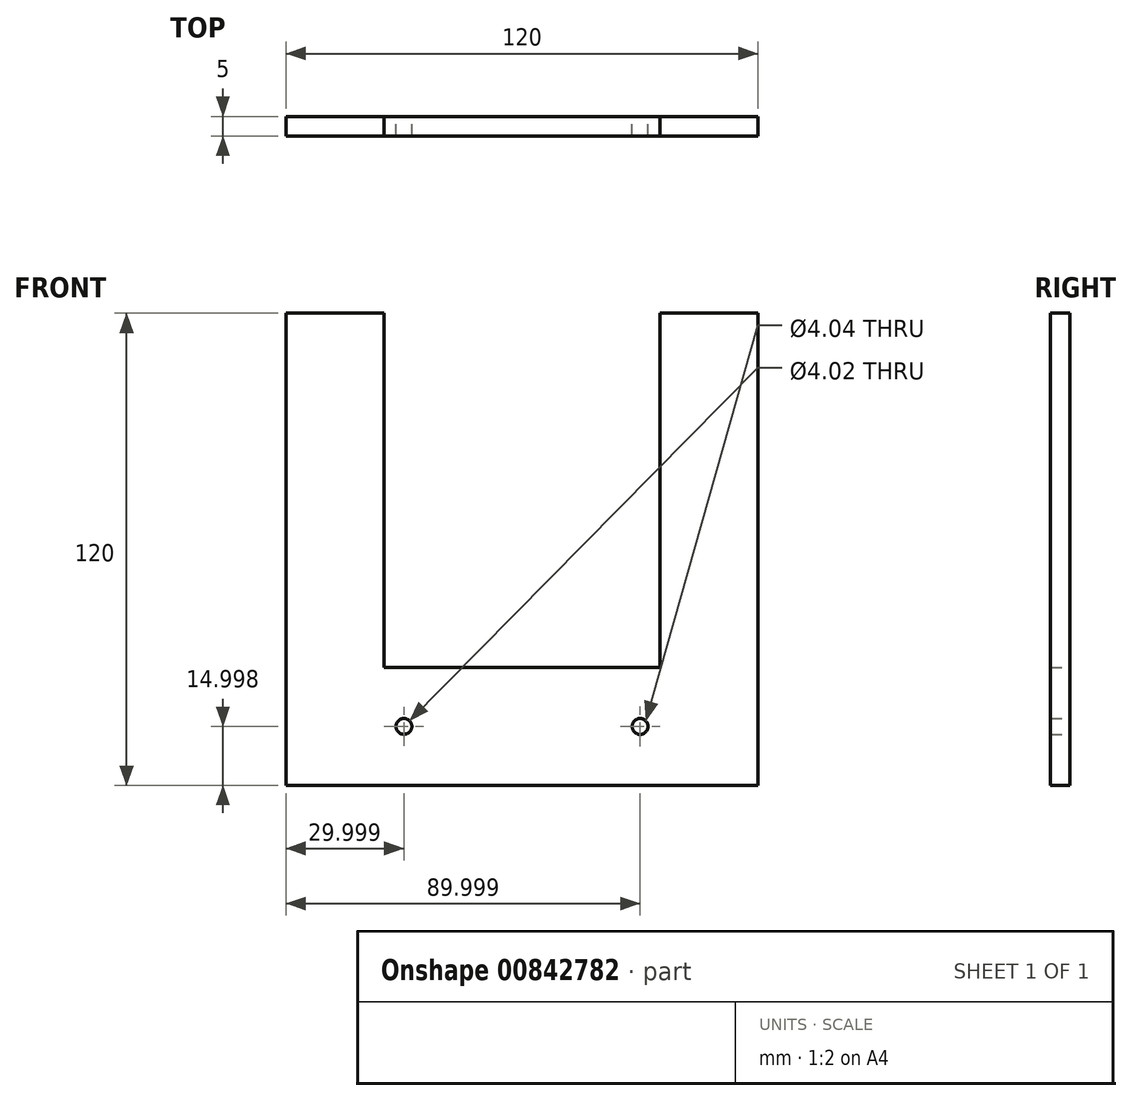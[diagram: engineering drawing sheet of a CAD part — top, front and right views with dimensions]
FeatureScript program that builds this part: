
annotation { "Feature Type Name" : "Feature", "Feature Type Description" : "" }
export const myFeature = defineFeature(function(context is Context, id is Id, definition is map)
    precondition{}
    {
        {
            var Q0;
            Q0=qCreatedBy(makeId("Front.planeOp"),FACE);
            var sketch = newSketch(context, id + "F0", { "sketchPlane" : qUnion([Q0])});
            skLineSegment(sketch, "E0", {"start": v(-60.14, -25.68) * mm, "end": v(59.86, -25.68) * mm});
            skPoint(sketch, "E1.end.orphan", {"position": v(59.86, 4.32) * mm});
            skLineSegment(sketch, "E2", {"start": v(59.86, -10.68) * mm, "end": v(59.86, 4.32) * mm});
            skLineSegment(sketch, "E3", {"start": v(-35.14, 4.32) * mm, "end": v(34.86, 4.32) * mm});
            skLineSegment(sketch, "E4", {"start": v(-32.15, -10.68) * mm, "end": v(-30.14, -10.68) * mm});
            skCircle(sketch, "E5", {"center": v(29.86, -10.68) * mm, "radius": 2.02 * mm});
            skPoint(sketch, "E6.orphan", {"position": v(59.86, -10.68) * mm});
            skLineSegment(sketch, "E7.trimOffspring", {"start": v(27.84, -10.68) * mm, "end": v(29.86, -10.68) * mm});
            skCircle(sketch, "E8", {"center": v(-30.14, -10.68) * mm, "radius": 2 * mm});
            skPoint(sketch, "E9.end.orphan", {"position": v(-60.14, -10.68) * mm});
            skLineSegment(sketch, "E10", {"start": v(-60.14, -25.68) * mm, "end": v(-60.14, 94.32) * mm});
            skLineSegment(sketch, "E11", {"start": v(59.86, -25.68) * mm, "end": v(59.86, 94.32) * mm});
            skLineSegment(sketch, "E12", {"start": v(59.86, 94.32) * mm, "end": v(34.86, 94.32) * mm});
            skLineSegment(sketch, "E13", {"start": v(-60.14, 94.32) * mm, "end": v(-35.14, 94.32) * mm});
            skLineSegment(sketch, "E14", {"start": v(-35.14, 94.32) * mm, "end": v(-35.14, 4.32) * mm});
            skLineSegment(sketch, "E15", {"start": v(34.86, 94.32) * mm, "end": v(34.86, 4.32) * mm});
            skPoint(sketch, "E16.orphan", {"position": v(-60.14, 4.32) * mm});
            skSolve(sketch);
        }
        {
            var Q0;
            Q0 = qSketchRegion(id + "F0", true);
            extrude(context, id + "F1", {"entities" : qUnion([Q0]), "depth" : 5 * mm, "offsetDistance" : 25 * mm});
        }
    });
